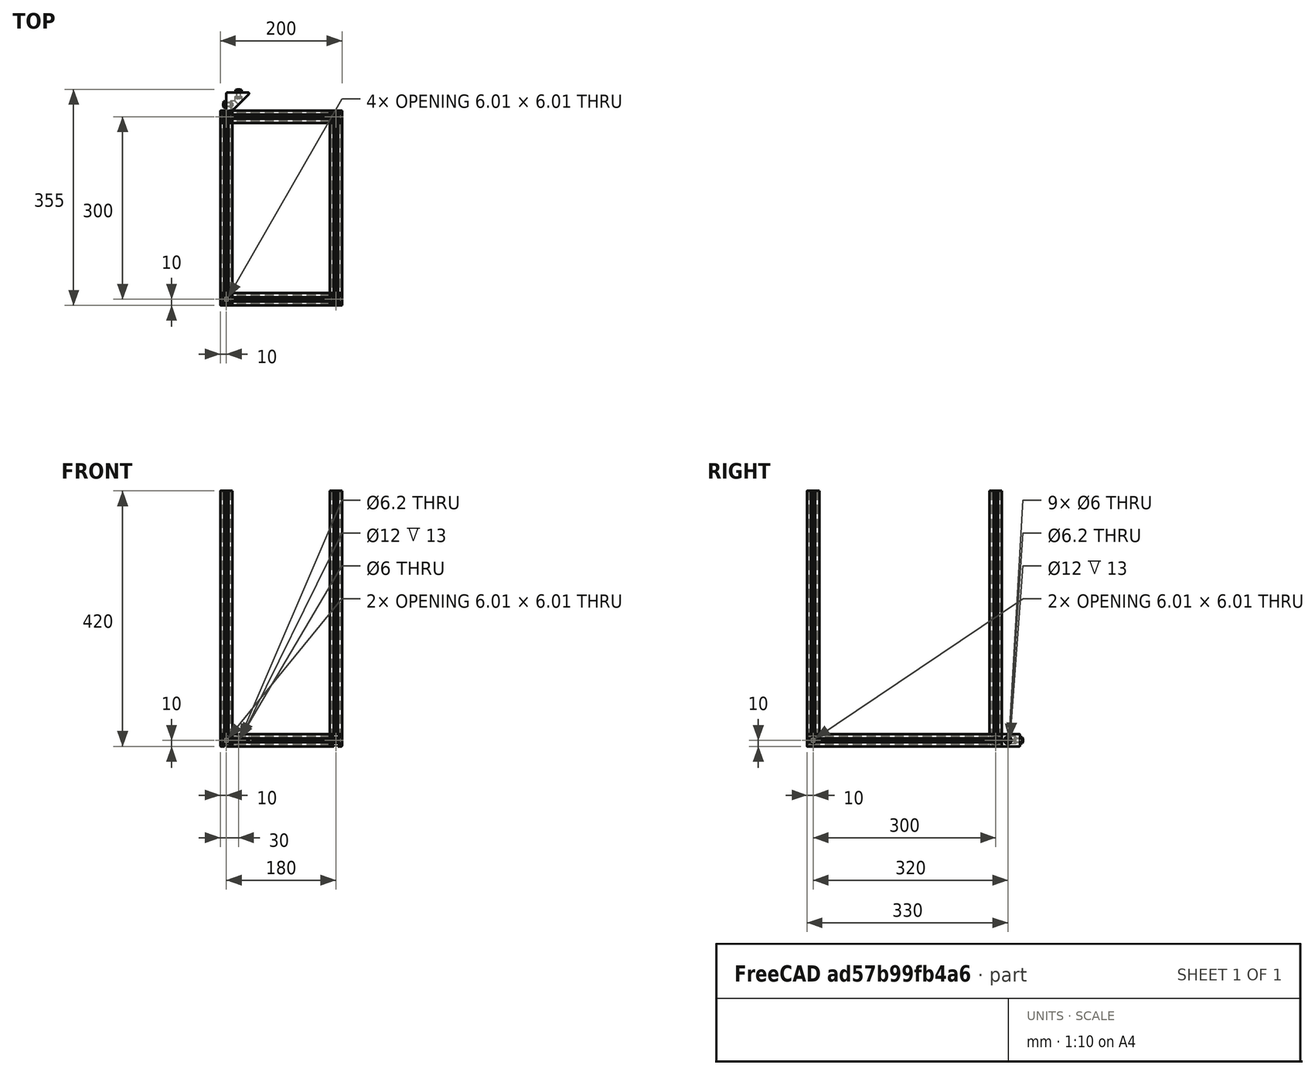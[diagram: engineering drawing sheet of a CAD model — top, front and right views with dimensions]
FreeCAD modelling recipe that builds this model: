
FCSTD DOCUMENT  (FreeCAD 0.17R9796 (Git))
Label: UPKframe4
License: All rights reserved
LicenseURL: http://en.wikipedia.org/wiki/All_rights_reserved
objects: Part::Feature×24, Part::FeaturePython×16, App::Part×6
note: 40 computed .brp shape members not serialized (recipe doc carries the construction recipe); baked Part::Feature solids carry a one-line shape summary decoded from their .brp

FEATURE [Part::Feature] Pocket001001  label="tslot40"
  Placement = pos=(0,0,20) rot=(0,0,1;0rad)
  shape: bbox 20 x 20 x 400 mm, 94 faces (baked)
FEATURE [Part::Feature] Pocket003001  label="tslot32con"
  Placement = pos=(0,10,10) rot=(1,0,0;1.5708rad)
  shape: bbox 20 x 320 x 20 mm, 150 faces (baked)
FEATURE [Part::Feature] Pocket003002  label="tslot16"
  Placement = pos=(10,0,10) rot=(0,1,0;1.5708rad)
  shape: bbox 160 x 20 x 20 mm, 94 faces (baked)
FEATURE [Part::Feature] Pocket003006  label="tslot16_001"
  Placement = pos=(10,-300,10) rot=(0,1,0;1.5708rad)
  shape: bbox 160 x 20 x 20 mm, 94 faces (baked)
FEATURE [Part::Feature] Pocket003007  label="tslot32con_001"
  Placement = pos=(180,-310,10) rot=(0,0.707107,0.707107;3.14159rad)
  shape: bbox 20 x 320 x 20 mm, 150 faces (baked)
FEATURE [Part::FeaturePython] Screw  label="M6x25-Screw"  # Fasteners workbench fastener (typed FeaturePython)
  Placement = pos=(-4,0,10) rot=(0,-1,0;1.5708rad)
  diameter = 7
  invert = false
  length = 6
  matchOuter = false
  offset = 0
  thread = false
  type = 15
FEATURE [Part::FeaturePython] Screw001  label="M6x25-Screw004"  # Fasteners workbench fastener (typed FeaturePython)
  Placement = pos=(-4,-300,10) rot=(0,-1,0;1.5708rad)
  diameter = 7
  invert = false
  length = 6
  matchOuter = false
  offset = 0
  thread = false
  type = 15
FEATURE [Part::FeaturePython] Screw002  label="M6x25-Screw005"  # Fasteners workbench fastener (typed FeaturePython)
  Placement = pos=(184,0,10) rot=(0,1,0;1.5708rad)
  diameter = 7
  invert = false
  length = 6
  matchOuter = false
  offset = 0
  thread = false
  type = 15
FEATURE [Part::FeaturePython] Screw004  label="M6x25-Screw006"  # Fasteners workbench fastener (typed FeaturePython)
  Placement = pos=(184,-300,10) rot=(0,1,0;1.5708rad)
  diameter = 7
  invert = false
  length = 6
  matchOuter = false
  offset = 0
  thread = false
  type = 15
FEATURE [App::Part] Part  label="lower_frame"
  Group = -> [Pocket003001,Pocket003002,Pocket003006,Pocket003007,Screw,Screw001,Screw002,Screw004]
  License = CC BY 3.0
  LicenseURL = http://creativecommons.org/licenses/by/3.0/
  Origin = -> PartOrigin
FEATURE [Part::Feature] Pocket003008  label="tslot32con001"
  Placement = pos=(0,10,10) rot=(1,0,0;1.5708rad)
  shape: bbox 20 x 320 x 20 mm, 150 faces (baked)
FEATURE [Part::Feature] Pocket003009  label="tslot041"
  Placement = pos=(10,0,10) rot=(0,1,0;1.5708rad)
  shape: bbox 160 x 20 x 20 mm, 94 faces (baked)
FEATURE [Part::Feature] Pocket003010  label="tslot16_002"
  Placement = pos=(10,-300,10) rot=(0,1,0;1.5708rad)
  shape: bbox 160 x 20 x 20 mm, 94 faces (baked)
FEATURE [Part::Feature] Pocket003011  label="tslot32con_002"
  Placement = pos=(180,-310,10) rot=(0,0.707107,0.707107;3.14159rad)
  shape: bbox 20 x 320 x 20 mm, 150 faces (baked)
FEATURE [Part::FeaturePython] Screw005  label="M6x25-Screw007"  # Fasteners workbench fastener (typed FeaturePython)
  Placement = pos=(-4,0,10) rot=(0,-1,0;1.5708rad)
  diameter = 7
  invert = false
  length = 6
  matchOuter = false
  offset = 0
  thread = false
  type = 15
FEATURE [Part::FeaturePython] Screw006  label="M6x25-Screw008"  # Fasteners workbench fastener (typed FeaturePython)
  Placement = pos=(-4,-300,10) rot=(0,-1,0;1.5708rad)
  diameter = 7
  invert = false
  length = 6
  matchOuter = false
  offset = 0
  thread = false
  type = 15
FEATURE [Part::FeaturePython] Screw007  label="M6x25-Screw009"  # Fasteners workbench fastener (typed FeaturePython)
  Placement = pos=(184,0,10) rot=(0,1,0;1.5708rad)
  diameter = 7
  invert = false
  length = 6
  matchOuter = false
  offset = 0
  thread = false
  type = 15
FEATURE [Part::FeaturePython] Screw008  label="M6x25-Screw010"  # Fasteners workbench fastener (typed FeaturePython)
  Placement = pos=(184,-300,10) rot=(0,1,0;1.5708rad)
  diameter = 7
  invert = false
  length = 6
  matchOuter = false
  offset = 0
  thread = false
  type = 15
FEATURE [App::Part] Part001  label="upper_frame"
  Group = -> [Pocket003008,Pocket003009,Pocket003010,Pocket003011,Screw005,Screw006,Screw007,Screw008]
  License = CC BY 3.0
  LicenseURL = http://creativecommons.org/licenses/by/3.0/
  Origin = -> PartOrigin001
  Placement = pos=(0,0,420) rot=(0,0,1;0rad)
FEATURE [Part::Feature] Pocket003012  label="tslot042"
  Placement = pos=(180,0,20) rot=(0,0,1;0rad)
  shape: bbox 20 x 20 x 400 mm, 94 faces (baked)
FEATURE [Part::Feature] Pocket003013  label="tslot043"
  Placement = pos=(180,-300,20) rot=(0,0,1;0rad)
  shape: bbox 20 x 20 x 400 mm, 94 faces (baked)
FEATURE [Part::Feature] Pocket003014  label="tslot044"
  Placement = pos=(0,-300,20) rot=(0,0,1;0rad)
  shape: bbox 20 x 20 x 400 mm, 94 faces (baked)
FEATURE [Part::Feature] Fillet004001  label="Fillet005"
  shape: bbox 37.5 x 37.5 x 20 mm, 26 faces (baked)
FEATURE [Part::FeaturePython] Screw009  label="M6x12-Screw"  # Fasteners workbench fastener (typed FeaturePython)
  Placement = pos=(7,20,10) rot=(0,1,0;1.5708rad)
  diameter = 4
  invert = false
  length = 1
  matchOuter = false
  offset = 0
  thread = false
  type = 20
FEATURE [Part::Feature] Body001  label="m6nutplate"
  Placement = pos=(-1.5,15,5) rot=(0,-1,0;1.5708rad)
  shape: bbox 3 x 10 x 10 mm, 9 faces (baked)
FEATURE [Part::FeaturePython] Screw010  label="M6x12-Screw001"  # Fasteners workbench fastener (typed FeaturePython)
  Placement = pos=(20,33,10) rot=(1,0,0;1.5708rad)
  diameter = 4
  invert = false
  length = 1
  matchOuter = false
  offset = 0
  thread = false
  type = 20
FEATURE [Part::Feature] Body002  label="m6nutplate001"
  Placement = pos=(15,41.5,5) rot=(0.57735,0.57735,0.57735;4.18879rad)
  shape: bbox 10 x 3 x 10 mm, 9 faces (baked)
FEATURE [App::Part] Part002  label="cornerstonescrewnut"
  Group = -> [Body001,Screw009,Fillet004001,Screw010,Body002]
  License = CC BY 3.0
  LicenseURL = http://creativecommons.org/licenses/by/3.0/
  Origin = -> PartOrigin002
  Placement = pos=(10,-50,20) rot=(0,-1,0;1.5708rad)
FEATURE [Part::Feature] Fillet004002  label="Fillet006"
  shape: bbox 37.5 x 37.5 x 20 mm, 26 faces (baked)
FEATURE [Part::FeaturePython] Screw011  label="M6x12-Screw002"  # Fasteners workbench fastener (typed FeaturePython)
  Placement = pos=(7,20,10) rot=(0,1,0;1.5708rad)
  diameter = 4
  invert = false
  length = 1
  matchOuter = false
  offset = 0
  thread = false
  type = 20
FEATURE [Part::Feature] Body003  label="m6nutplate002"
  Placement = pos=(-1.5,15,5) rot=(0,-1,0;1.5708rad)
  shape: bbox 3 x 10 x 10 mm, 9 faces (baked)
FEATURE [Part::FeaturePython] Screw012  label="M6x12-Screw003"  # Fasteners workbench fastener (typed FeaturePython)
  Placement = pos=(20,33,10) rot=(1,0,0;1.5708rad)
  diameter = 4
  invert = false
  length = 1
  matchOuter = false
  offset = 0
  thread = false
  type = 20
FEATURE [Part::Feature] Body004  label="m6nutplate003"
  Placement = pos=(15,41.5,5) rot=(0.57735,0.57735,0.57735;4.18879rad)
  shape: bbox 10 x 3 x 10 mm, 9 faces (baked)
FEATURE [App::Part] Part003  label="cornerstonescrewnut001"
  Group = -> [Body003,Screw011,Fillet004002,Screw012,Body004]
  License = CC BY 3.0
  LicenseURL = http://creativecommons.org/licenses/by/3.0/
  Origin = -> PartOrigin003
  Placement = pos=(190,-50,20) rot=(0,-1,0;1.5708rad)
FEATURE [Part::Feature] Fillet004003  label="Fillet007"
  shape: bbox 37.5 x 37.5 x 20 mm, 26 faces (baked)
FEATURE [Part::FeaturePython] Screw013  label="M6x12-Screw004"  # Fasteners workbench fastener (typed FeaturePython)
  Placement = pos=(7,20,10) rot=(0,1,0;1.5708rad)
  diameter = 4
  invert = false
  length = 1
  matchOuter = false
  offset = 0
  thread = false
  type = 20
FEATURE [Part::Feature] Body005  label="m6nutplate004"
  Placement = pos=(-1.5,15,5) rot=(0,-1,0;1.5708rad)
  shape: bbox 3 x 10 x 10 mm, 9 faces (baked)
FEATURE [Part::FeaturePython] Screw014  label="M6x12-Screw005"  # Fasteners workbench fastener (typed FeaturePython)
  Placement = pos=(20,33,10) rot=(1,0,0;1.5708rad)
  diameter = 4
  invert = false
  length = 1
  matchOuter = false
  offset = 0
  thread = false
  type = 20
FEATURE [Part::Feature] Body006  label="m6nutplate005"
  Placement = pos=(15,41.5,5) rot=(0.57735,0.57735,0.57735;4.18879rad)
  shape: bbox 10 x 3 x 10 mm, 9 faces (baked)
FEATURE [App::Part] Part004  label="cornerstonescrewnut002"
  Group = -> [Body005,Screw013,Fillet004003,Screw014,Body006]
  License = CC BY 3.0
  LicenseURL = http://creativecommons.org/licenses/by/3.0/
  Origin = -> PartOrigin004
  Placement = pos=(-10,-50,420) rot=(0,1,0;1.5708rad)
FEATURE [Part::Feature] Fillet004004  label="Fillet008"
  shape: bbox 37.5 x 37.5 x 20 mm, 26 faces (baked)
FEATURE [Part::FeaturePython] Screw015  label="M6x12-Screw006"  # Fasteners workbench fastener (typed FeaturePython)
  Placement = pos=(7,20,10) rot=(0,1,0;1.5708rad)
  diameter = 4
  invert = false
  length = 1
  matchOuter = false
  offset = 0
  thread = false
  type = 20
FEATURE [Part::Feature] Body007  label="m6nutplate006"
  Placement = pos=(-1.5,15,5) rot=(0,-1,0;1.5708rad)
  shape: bbox 3 x 10 x 10 mm, 9 faces (baked)
FEATURE [Part::FeaturePython] Screw016  label="M6x12-Screw007"  # Fasteners workbench fastener (typed FeaturePython)
  Placement = pos=(20,33,10) rot=(1,0,0;1.5708rad)
  diameter = 4
  invert = false
  length = 1
  matchOuter = false
  offset = 0
  thread = false
  type = 20
FEATURE [Part::Feature] Body008  label="m6nutplate007"
  Placement = pos=(15,41.5,5) rot=(0.57735,0.57735,0.57735;4.18879rad)
  shape: bbox 10 x 3 x 10 mm, 9 faces (baked)
FEATURE [App::Part] Part005  label="cornerstonescrewnut003"
  Group = -> [Body007,Screw015,Fillet004004,Screw016,Body008]
  License = CC BY 3.0
  LicenseURL = http://creativecommons.org/licenses/by/3.0/
  Origin = -> PartOrigin005
  Placement = pos=(170,-50,420) rot=(0,1,0;1.5708rad)
